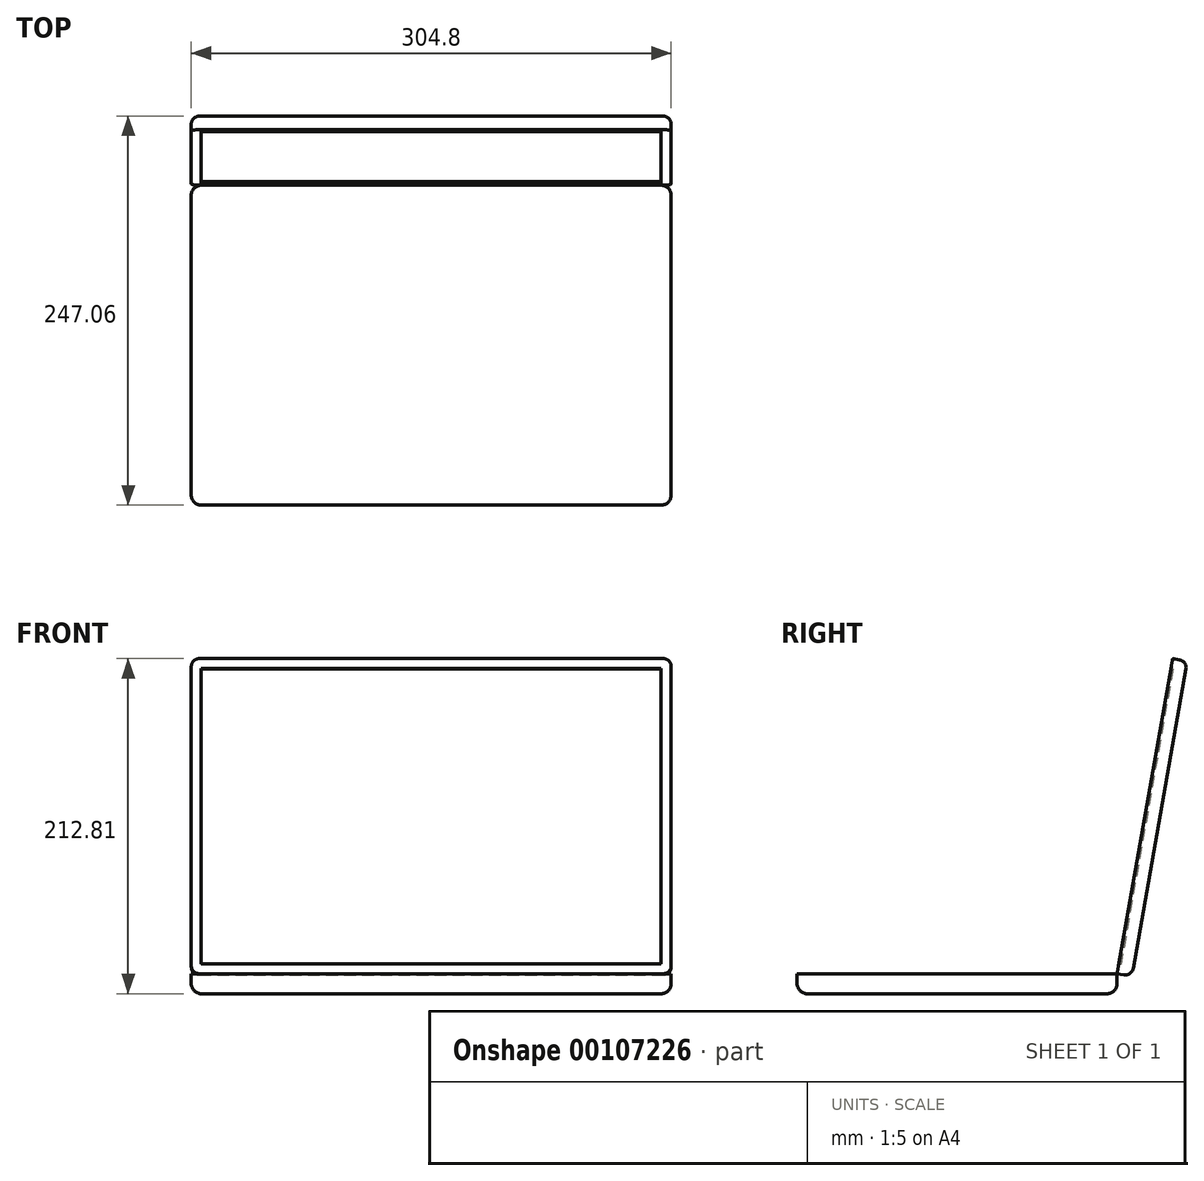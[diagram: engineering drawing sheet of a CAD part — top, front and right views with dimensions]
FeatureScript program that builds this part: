
annotation { "Feature Type Name" : "Feature", "Feature Type Description" : "" }
export const myFeature = defineFeature(function(context is Context, id is Id, definition is map)
    precondition{}
    {
        {
            var Q0;
            Q0=qCreatedBy(makeId("Top.planeOp"),FACE);
            var sketch = newSketch(context, id + "F0", { "sketchPlane" : qUnion([Q0])});
            skLineSegment(sketch, "E0.bottom", {"start": v(-152.4, 0) * mm, "end": v(152.4, 0) * mm});
            skLineSegment(sketch, "E0.top", {"start": v(-152.4, 203.2) * mm, "end": v(152.4, 203.2) * mm});
            skLineSegment(sketch, "E0.left", {"start": v(-152.4, 0) * mm, "end": v(-152.4, 203.2) * mm});
            skLineSegment(sketch, "E0.right", {"start": v(152.4, 0) * mm, "end": v(152.4, 203.2) * mm});
            skSolve(sketch);
        }
        {
            var Q0;
            Q0 = qSketchRegion(id + "F0", true);
            extrude(context, id + "F1", {"entities" : qUnion([Q0]), "depth" : 12.7 * mm});
        }
        {
            var Q0;
            Q0=makeQuery(id+"F1.opExtrude","CAP_FACE",FACE,{"disambiguationData":[OSD([sQuery(id+"F0.wireOp",EDGE,"E0.bottom"),sQuery(id+"F0.wireOp",EDGE,"E0.top"),sQuery(id+"F0.wireOp",EDGE,"E0.left"),sQuery(id+"F0.wireOp",EDGE,"E0.right")])],"isStart":false});
            var sketch = newSketch(context, id + "F2", { "sketchPlane" : qUnion([Q0])});
            skLineSegment(sketch, "E1.bottom", {"start": v(-152.4, 0) * mm, "end": v(152.4, 0) * mm});
            skLineSegment(sketch, "E1.top", {"start": v(-152.4, 203.2) * mm, "end": v(152.4, 203.2) * mm});
            skLineSegment(sketch, "E1.left", {"start": v(-152.4, 0) * mm, "end": v(-152.4, 203.2) * mm});
            skLineSegment(sketch, "E1.right", {"start": v(152.4, 0) * mm, "end": v(152.4, 203.2) * mm});
            skSolve(sketch);
        }
        {
            var Q0;
            Q0 = qSketchRegion(id + "F2", true);
            extrude(context, id + "F3", {"entities" : qUnion([Q0]), "depth" : 9.52 * mm});
        }
        {
            var Q0;
            Q0=makeQuery(id+"F3.opExtrude","SWEPT_BODY",BODY,{"disambiguationData":[OSD([sQuery(id+"F2.wireOp",EDGE,"E1.bottom"),sQuery(id+"F2.wireOp",EDGE,"E1.top"),sQuery(id+"F2.wireOp",EDGE,"E1.left"),sQuery(id+"F2.wireOp",EDGE,"E1.right")])]});
            var Q1;
            Q1=makeQuery(id+"F3.opExtrude","CAP_EDGE",EDGE,{"disambiguationData":[OSD([sQuery(id+"F2.wireOp",EDGE,"E1.top")])],"isStart":true});
            transform(context, id + "F4", {"entities" : qUnion([Q0]), "transformType" : TransformType.ROTATION, "transformAxis" : qUnion([Q1]), "angle" : 100 * degree, "oppositeDirection" : true, "makeCopy" : false});
        }
        {
            var Q0;
            Q0=makeQuery(id+"F3.opExtrude","CAP_FACE",FACE,{"disambiguationData":[OSD([sQuery(id+"F2.wireOp",EDGE,"E1.bottom"),sQuery(id+"F2.wireOp",EDGE,"E1.top"),sQuery(id+"F2.wireOp",EDGE,"E1.left"),sQuery(id+"F2.wireOp",EDGE,"E1.right")])],"isStart":true});
            var sketch = newSketch(context, id + "F5", { "sketchPlane" : qUnion([Q0])});
            skLineSegment(sketch, "E2.0", {"start": v(-146.05, 244.64) * mm, "end": v(-146.05, 54.14) * mm});
            skLineSegment(sketch, "E2.1", {"start": v(146.05, 244.64) * mm, "end": v(-146.05, 244.64) * mm});
            skLineSegment(sketch, "E2.2", {"start": v(146.05, 54.14) * mm, "end": v(146.05, 244.64) * mm});
            skLineSegment(sketch, "E2.3", {"start": v(-146.05, 54.14) * mm, "end": v(146.05, 54.14) * mm});
            skSolve(sketch);
        }
        {
            var Q0;
            Q0 = qSketchRegion(id + "F5", true);
            extrude(context, id + "F6", {"entities" : qUnion([Q0]), "operationType" : NewBodyOperationType.REMOVE, "oppositeDirection" : true, "depth" : 1.27 * mm});
        }
        {
            var Q0;
            Q0=makeQuery(id+"F1.opExtrude","CAP_FACE",FACE,{"disambiguationData":[OSD([sQuery(id+"F0.wireOp",EDGE,"E0.bottom"),sQuery(id+"F0.wireOp",EDGE,"E0.top"),sQuery(id+"F0.wireOp",EDGE,"E0.left"),sQuery(id+"F0.wireOp",EDGE,"E0.right")])],"isStart":true});
            var Q1;
            Q1=makeQuery(id+"F1.opExtrude","SWEPT_EDGE",EDGE,{"disambiguationData":[OSD([sQuery(id+"F0.wireOp",EDGE,"E0.bottom"),sQuery(id+"F0.wireOp",EDGE,"E0.right")])]});
            var Q2;
            Q2=makeQuery(id+"F1.opExtrude","SWEPT_EDGE",EDGE,{"disambiguationData":[OSD([sQuery(id+"F0.wireOp",EDGE,"E0.top"),sQuery(id+"F0.wireOp",EDGE,"E0.right")])]});
            var Q3;
            Q3=makeQuery(id+"F1.opExtrude","SWEPT_EDGE",EDGE,{"disambiguationData":[OSD([sQuery(id+"F0.wireOp",EDGE,"E0.bottom"),sQuery(id+"F0.wireOp",EDGE,"E0.left")])]});
            var Q4;
            Q4=makeQuery(id+"F1.opExtrude","SWEPT_EDGE",EDGE,{"disambiguationData":[OSD([sQuery(id+"F0.wireOp",EDGE,"E0.top"),sQuery(id+"F0.wireOp",EDGE,"E0.left")])]});
            fillet(context, id + "F7", {"entities" : qUnion([Q0, Q1, Q2, Q3, Q4]), "radius" : 6.35 * mm, "tangentPropagation" : true, "allowEdgeOverflow" : false});
        }
        {
            var Q0;
            Q0=makeQuery(id+"F3.opExtrude","CAP_FACE",FACE,{"disambiguationData":[OSD([sQuery(id+"F2.wireOp",EDGE,"E1.bottom"),sQuery(id+"F2.wireOp",EDGE,"E1.top"),sQuery(id+"F2.wireOp",EDGE,"E1.left"),sQuery(id+"F2.wireOp",EDGE,"E1.right")])],"isStart":false});
            var Q1;
            Q1=makeQuery(id+"F3.opExtrude","SWEPT_EDGE",EDGE,{"disambiguationData":[OSD([sQuery(id+"F2.wireOp",EDGE,"E1.bottom"),sQuery(id+"F2.wireOp",EDGE,"E1.right")])]});
            var Q2;
            Q2=makeQuery(id+"F3.opExtrude","SWEPT_EDGE",EDGE,{"disambiguationData":[OSD([sQuery(id+"F2.wireOp",EDGE,"E1.top"),sQuery(id+"F2.wireOp",EDGE,"E1.right")])]});
            var Q3;
            Q3=makeQuery(id+"F3.opExtrude","SWEPT_EDGE",EDGE,{"disambiguationData":[OSD([sQuery(id+"F2.wireOp",EDGE,"E1.bottom"),sQuery(id+"F2.wireOp",EDGE,"E1.left")])]});
            var Q4;
            Q4=makeQuery(id+"F3.opExtrude","SWEPT_EDGE",EDGE,{"disambiguationData":[OSD([sQuery(id+"F2.wireOp",EDGE,"E1.top"),sQuery(id+"F2.wireOp",EDGE,"E1.left")])]});
            fillet(context, id + "F8", {"entities" : qUnion([Q0, Q1, Q2, Q3, Q4]), "radius" : 5.08 * mm, "tangentPropagation" : true, "allowEdgeOverflow" : false});
        }
    });
